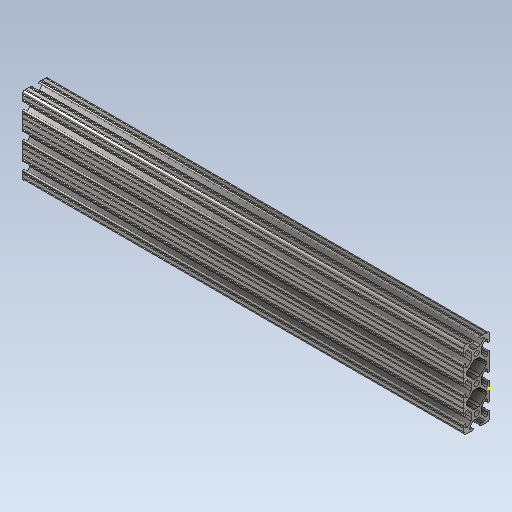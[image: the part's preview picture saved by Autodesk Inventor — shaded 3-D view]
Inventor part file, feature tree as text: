
AUTODESK INVENTOR PART (.ipt)
format: ipt  version: 2020 (Build 240168000, 168)  size: 416,256 bytes
history: native  units: in
note: dims shown in document units (in); Inventor stores cm internally (conversion verified against a paired STEP export)
features: sketch x2, extrude x1
ambient origin geometry x8: Origin, YZ Plane, XZ Plane, XY Plane, X Axis, Y Axis, Z Axis, Center Point
bodies: Solid1 (feature_tree)
feature tree (3):
  extrude  "Extrusion1"  [1 undecoded]
  sketch  "Sketch2"
  sketch  "Sketch1"  dims[d0=17.0in d1=0.0in]
note: 1 required parameter value undecoded (feature->parameter linkage not recoverable at this tier; creation-order binding heuristic only, values carry confidence <= 0.55)
